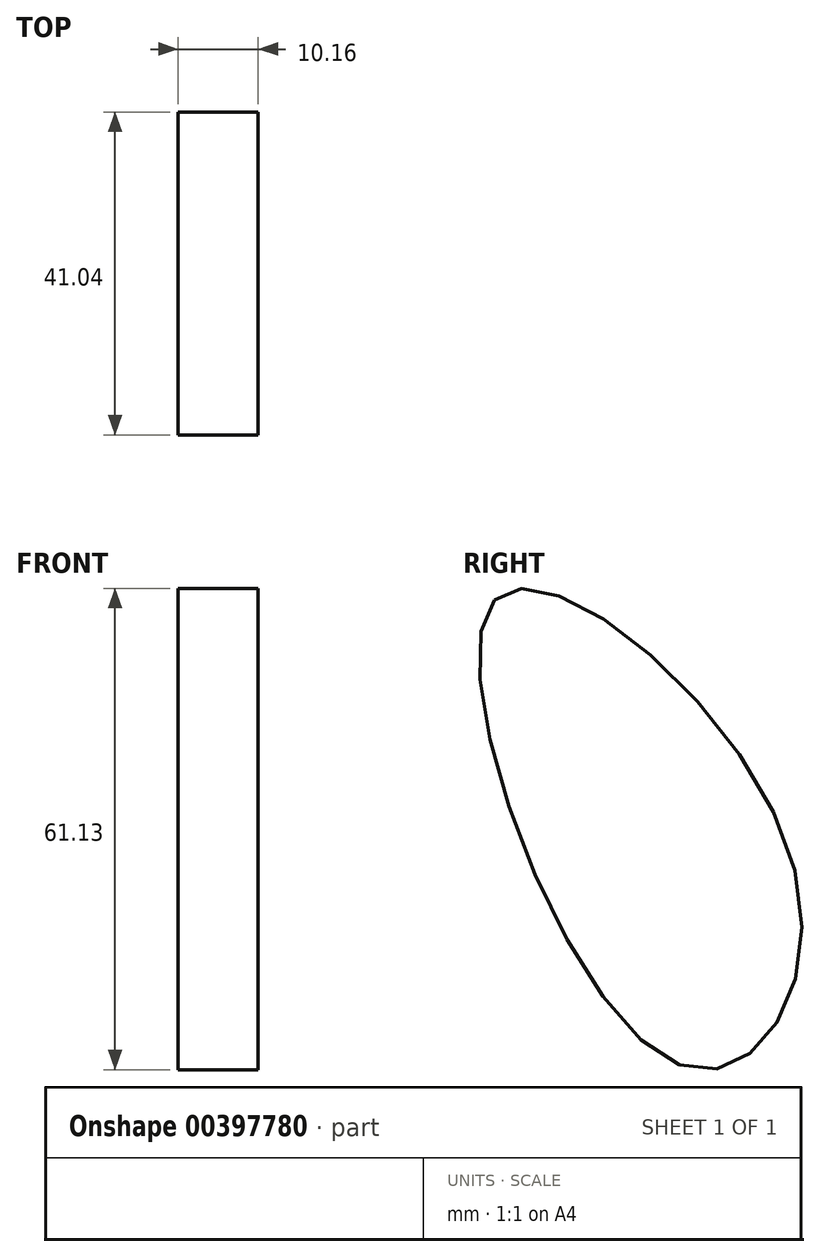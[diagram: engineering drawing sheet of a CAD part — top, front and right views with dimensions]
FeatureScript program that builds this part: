
annotation { "Feature Type Name" : "Feature", "Feature Type Description" : "" }
export const myFeature = defineFeature(function(context is Context, id is Id, definition is map)
    precondition{}
    {
        {
            var Q0;
            Q0=qCreatedBy(makeId("Right.planeOp"),FACE);
            var sketch = newSketch(context, id + "F0", { "sketchPlane" : qUnion([Q0])});
            skFitSpline(sketch, "E0", {"points": [v(-38.34, 45.42) * mm, v(-15.16, -13.53) * mm, v(0, 10.4) * mm, v(-38.34, 45.42) * mm]});
            skSolve(sketch);
        }
        {
            var Q0;
            Q0 = qSketchRegion(id + "F0", true);
            extrude(context, id + "F1", {"entities" : qUnion([Q0]), "depth" : 10.16 * mm});
        }
    });
